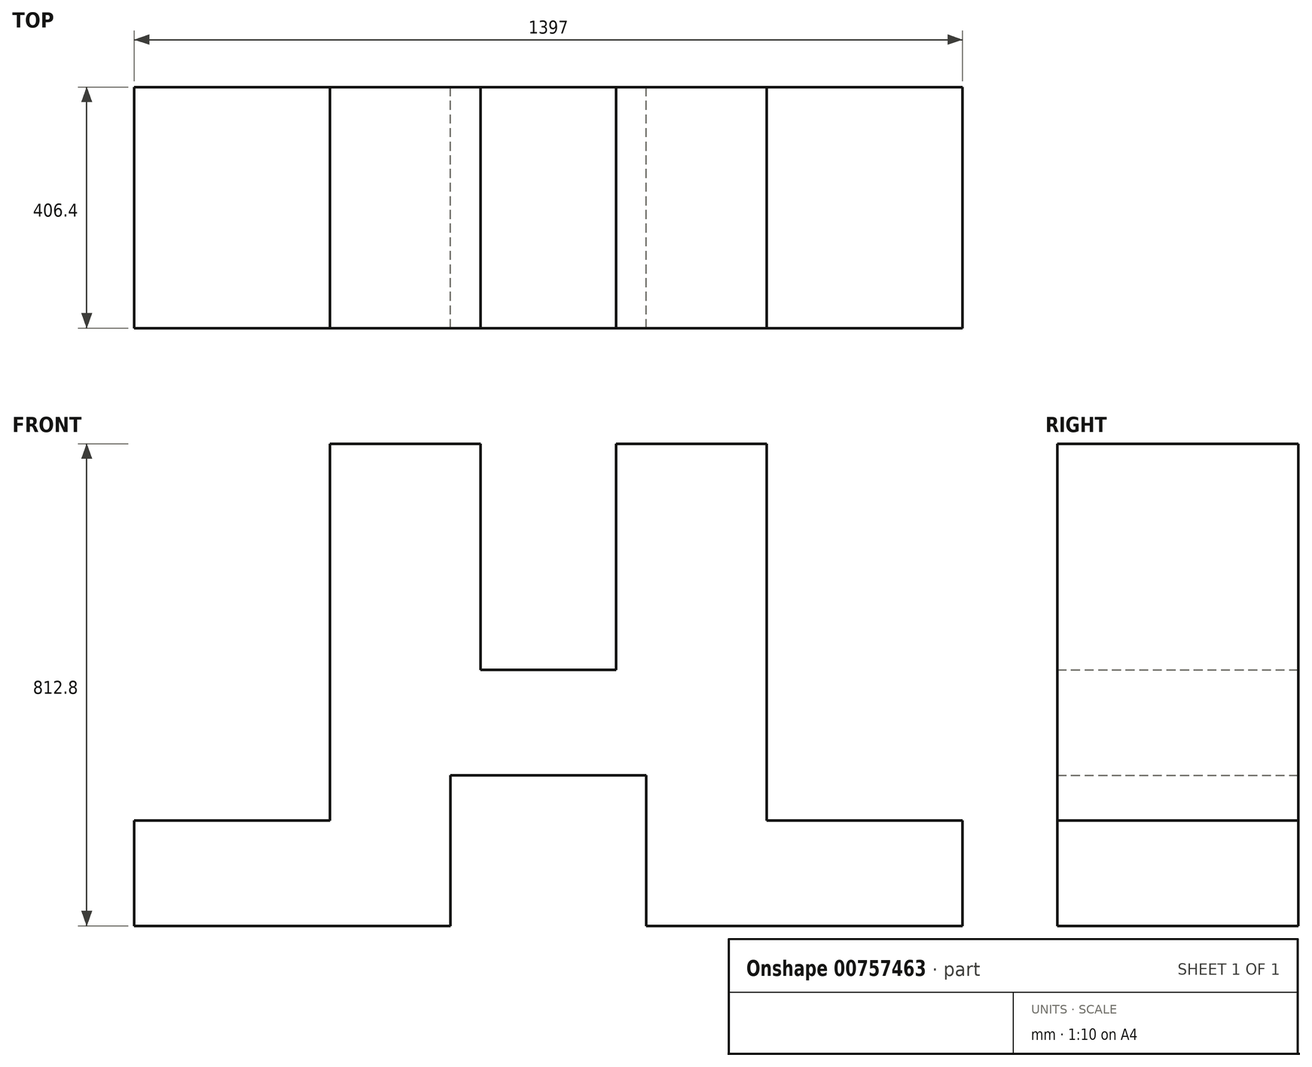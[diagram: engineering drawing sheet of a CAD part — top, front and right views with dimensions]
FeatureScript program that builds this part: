
annotation { "Feature Type Name" : "Feature", "Feature Type Description" : "" }
export const myFeature = defineFeature(function(context is Context, id is Id, definition is map)
    precondition{}
    {
        {
            var Q0;
            Q0=qCreatedBy(makeId("Front.planeOp"),FACE);
            var sketch = newSketch(context, id + "F0", { "sketchPlane" : qUnion([Q0])});
            skLineSegment(sketch, "E0", {"start": v(0, 0) * mm, "end": v(0, 177.8) * mm});
            skLineSegment(sketch, "E1", {"start": v(0, 177.8) * mm, "end": v(-330.2, 177.8) * mm});
            skLineSegment(sketch, "E2", {"start": v(-330.2, 177.8) * mm, "end": v(-330.2, 812.8) * mm});
            skLineSegment(sketch, "E3", {"start": v(-330.2, 812.8) * mm, "end": v(-584.2, 812.8) * mm});
            skLineSegment(sketch, "E4", {"start": v(-584.2, 812.8) * mm, "end": v(-584.2, 431.8) * mm});
            skLineSegment(sketch, "E5", {"start": v(-584.2, 431.8) * mm, "end": v(-812.8, 431.8) * mm});
            skLineSegment(sketch, "E6", {"start": v(-812.8, 431.8) * mm, "end": v(-812.8, 812.8) * mm});
            skLineSegment(sketch, "E7", {"start": v(-812.8, 812.8) * mm, "end": v(-1066.8, 812.8) * mm});
            skLineSegment(sketch, "E8", {"start": v(-1066.8, 812.8) * mm, "end": v(-1066.8, 177.8) * mm});
            skLineSegment(sketch, "E9", {"start": v(-1066.8, 177.8) * mm, "end": v(-1397, 177.8) * mm});
            skLineSegment(sketch, "E10", {"start": v(-1397, 177.8) * mm, "end": v(-1397, 0) * mm});
            skLineSegment(sketch, "E11", {"start": v(-1397, 0) * mm, "end": v(-863.6, 0) * mm});
            skLineSegment(sketch, "E12", {"start": v(-698.5, 254) * mm, "end": v(-533.4, 254) * mm});
            skLineSegment(sketch, "E13", {"start": v(-533.4, 254) * mm, "end": v(-533.4, 0) * mm});
            skLineSegment(sketch, "E14", {"start": v(-698.5, 254) * mm, "end": v(-863.6, 254) * mm});
            skLineSegment(sketch, "E15", {"start": v(-863.6, 254) * mm, "end": v(-863.6, 0) * mm});
            skLineSegment(sketch, "E16.trimOffspring", {"start": v(-533.4, 0) * mm, "end": v(0, 0) * mm});
            skSolve(sketch);
        }
        {
            var Q0;
            Q0=makeQuery(id+"F0.imprint","IMPRINT",FACE,{"disambiguationData":[TD([[makeQuery(id+"F0.imprint","IMPRINT",EDGE,{"derivedFrom":sQuery(id+"F0.wireOp",EDGE,"E0")}),1.0]])]});
            extrude(context, id + "F1", {"entities" : qUnion([Q0]), "depth" : 406.4 * mm, "offsetDistance" : 25.4 * mm});
        }
    });
